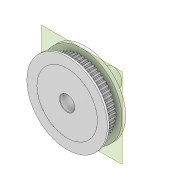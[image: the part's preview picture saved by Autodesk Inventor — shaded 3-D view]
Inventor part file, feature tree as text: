
AUTODESK INVENTOR PART (.ipt)
format: ipt  version: 2022 (Build 260153000, 153)  size: 1,102,336 bytes
history: native  units: in
note: dims shown in document units (in); Inventor stores cm internally (conversion verified against a paired STEP export)
features: extrude x4, sketch x4, plane x1
ambient origin geometry x8: Origin, YZ Plane, XZ Plane, XY Plane, X Axis, Y Axis, Z Axis, Center Point
bodies: Solid2 (feature_tree), Solid1 (feature_tree)
feature tree (9):
  plane  "Work Plane1"
  extrude  "Extrusion1"  Depth=3.937in TaperAngle=0.0deg
  extrude  "Extrusion2"  Depth=0.0787in
  extrude  "Extrusion3"  Depth=0.3937in
  extrude  "Extrusion4"  [1 undecoded]
  sketch  "Sketch1"  dims[d0=0.2559in d1=3.937in d2=0.0in]
  sketch  "Sketch2"  dims[d3=0.0787in d4=0.0in d5=0.1654in]
  sketch  "Sketch3"  dims[d6=3.937in d7=0.0in d8=0.3937in]
  sketch  "Sketch4"  dims[d9=0.5906in d10=0.0in]
note: 1 required parameter value undecoded (feature->parameter linkage not recoverable at this tier; creation-order binding heuristic only, values carry confidence <= 0.55)
